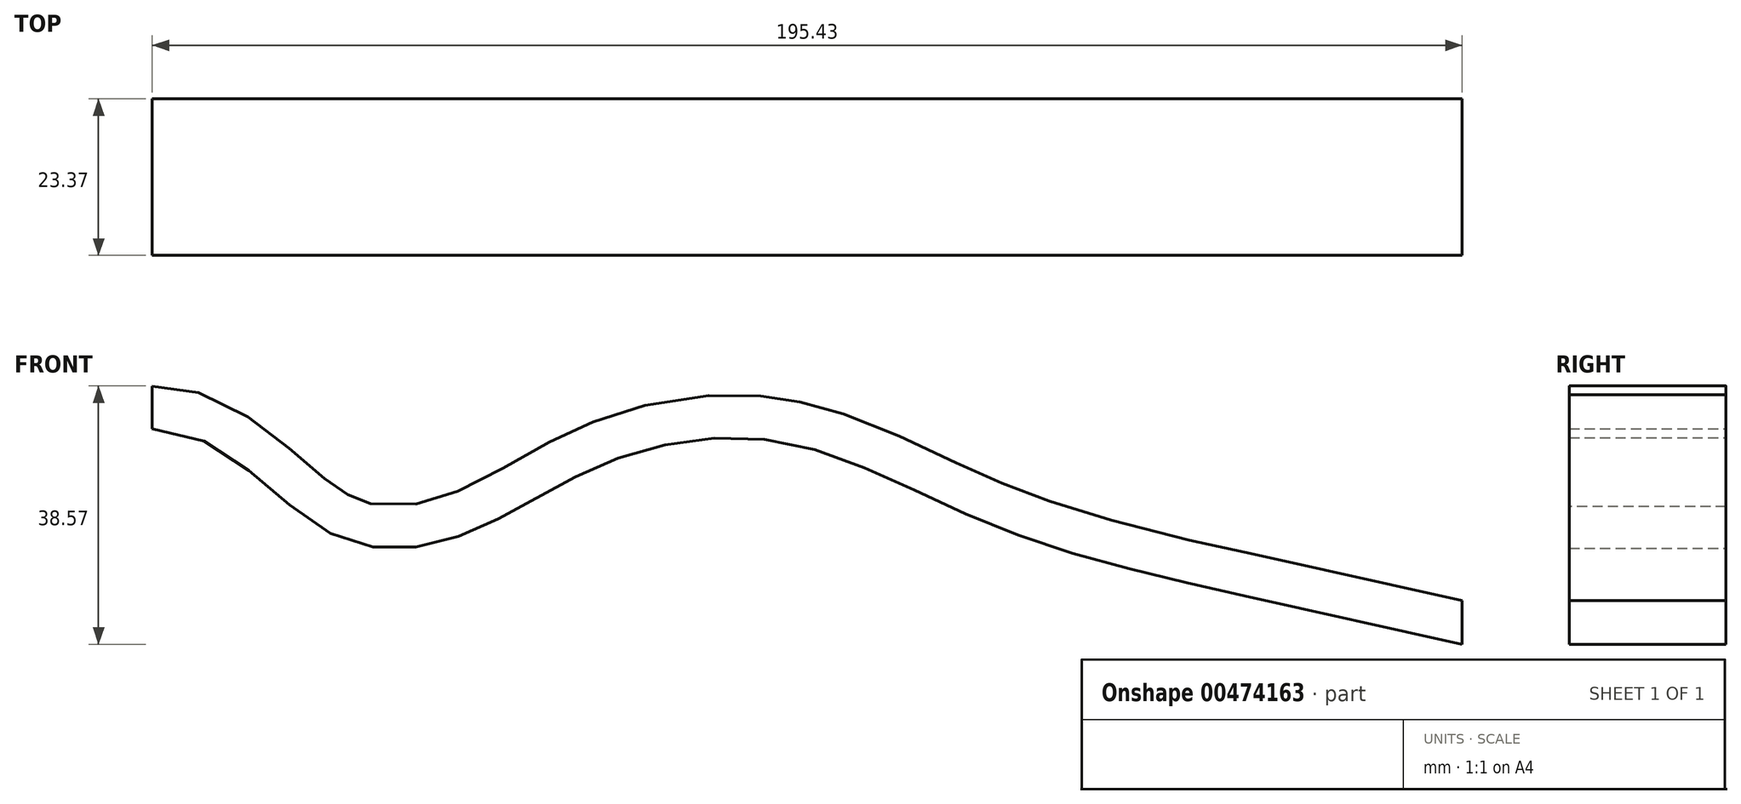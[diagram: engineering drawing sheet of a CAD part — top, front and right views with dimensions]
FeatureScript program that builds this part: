
annotation { "Feature Type Name" : "Feature", "Feature Type Description" : "" }
export const myFeature = defineFeature(function(context is Context, id is Id, definition is map)
    precondition{}
    {
        {
            var Q0;
            Q0=qCreatedBy(makeId("Front.planeOp"),FACE);
            var sketch = newSketch(context, id + "F0", { "sketchPlane" : qUnion([Q0])});
            skFitSpline(sketch, "E0", {"points": [v(0, 19.97) * mm, v(26.34, 4.4) * mm, v(47.05, 4.4) * mm, v(67, 14.57) * mm, v(94.1, 17.96) * mm, v(125.34, 5.54) * mm, v(162.99, -5) * mm], "startDerivative": vector(193.23, 0) * mm, "endDerivative": vector(199.48, -44.44) * mm});
            skLineSegment(sketch, "E1", {"start": v(162.99, -5) * mm, "end": v(195.43, -12.24) * mm});
            skLineSegment(sketch, "E2.0", {"start": v(164.37, 1.2) * mm, "end": v(195.43, -5.73) * mm});
            skFitSpline(sketch, "E2.1", {"points": [v(0, 26.32) * mm, v(1.4, 26.32) * mm, v(4.1, 26.07) * mm, v(7.85, 25.04) * mm, v(11.22, 23.56) * mm, v(14.24, 21.77) * mm, v(16.97, 19.83) * mm, v(19.46, 17.82) * mm, v(21.76, 15.84) * mm, v(23.9, 13.99) * mm, v(25.55, 12.62) * mm, v(26.8, 11.66) * mm, v(27.68, 11.02) * mm, v(28.38, 10.56) * mm, v(28.91, 10.24) * mm, v(29.3, 10.03) * mm, v(29.67, 9.83) * mm, v(30.18, 9.59) * mm, v(30.8, 9.32) * mm, v(31.57, 9.05) * mm, v(32.6, 8.76) * mm, v(34.44, 8.42) * mm, v(37.23, 8.36) * mm, v(40.22, 8.86) * mm, v(42.67, 9.56) * mm, v(44.52, 10.22) * mm, v(46.35, 11) * mm, v(48.83, 12.17) * mm, v(52.03, 13.9) * mm, v(55.45, 15.86) * mm, v(58.38, 17.47) * mm, v(60.69, 18.67) * mm, v(63.12, 19.83) * mm, v(65.71, 20.93) * mm, v(68.4, 21.92) * mm, v(72.09, 23.07) * mm, v(76.9, 24.2) * mm, v(81.9, 24.84) * mm, v(86, 25) * mm, v(89.1, 24.94) * mm, v(91.7, 24.73) * mm, v(93.78, 24.46) * mm, v(95.34, 24.2) * mm, v(96.9, 23.88) * mm, v(98.94, 23.4) * mm, v(101.44, 22.7) * mm, v(104.37, 21.7) * mm, v(108.2, 20.24) * mm, v(112.84, 18.2) * mm, v(117.38, 16.07) * mm, v(120.97, 14.39) * mm, v(123.65, 13.16) * mm, v(126.32, 12) * mm, v(128.98, 10.9) * mm, v(131.7, 9.88) * mm, v(135.4, 8.59) * mm, v(140.16, 7.1) * mm, v(146.02, 5.48) * mm, v(154.03, 3.5) * mm, v(160.21, 2.12) * mm, v(164.37, 1.2) * mm]});
            skLineSegment(sketch, "E3", {"start": v(0, 26.32) * mm, "end": v(0, 19.97) * mm});
            skLineSegment(sketch, "E4", {"start": v(195.43, -5.73) * mm, "end": v(195.43, -12.24) * mm});
            skSolve(sketch);
        }
        {
            var Q0;
            Q0 = qSketchRegion(id + "F0", true);
            extrude(context, id + "F1", {"entities" : qUnion([Q0]), "depth" : 23.37 * mm});
        }
    });
